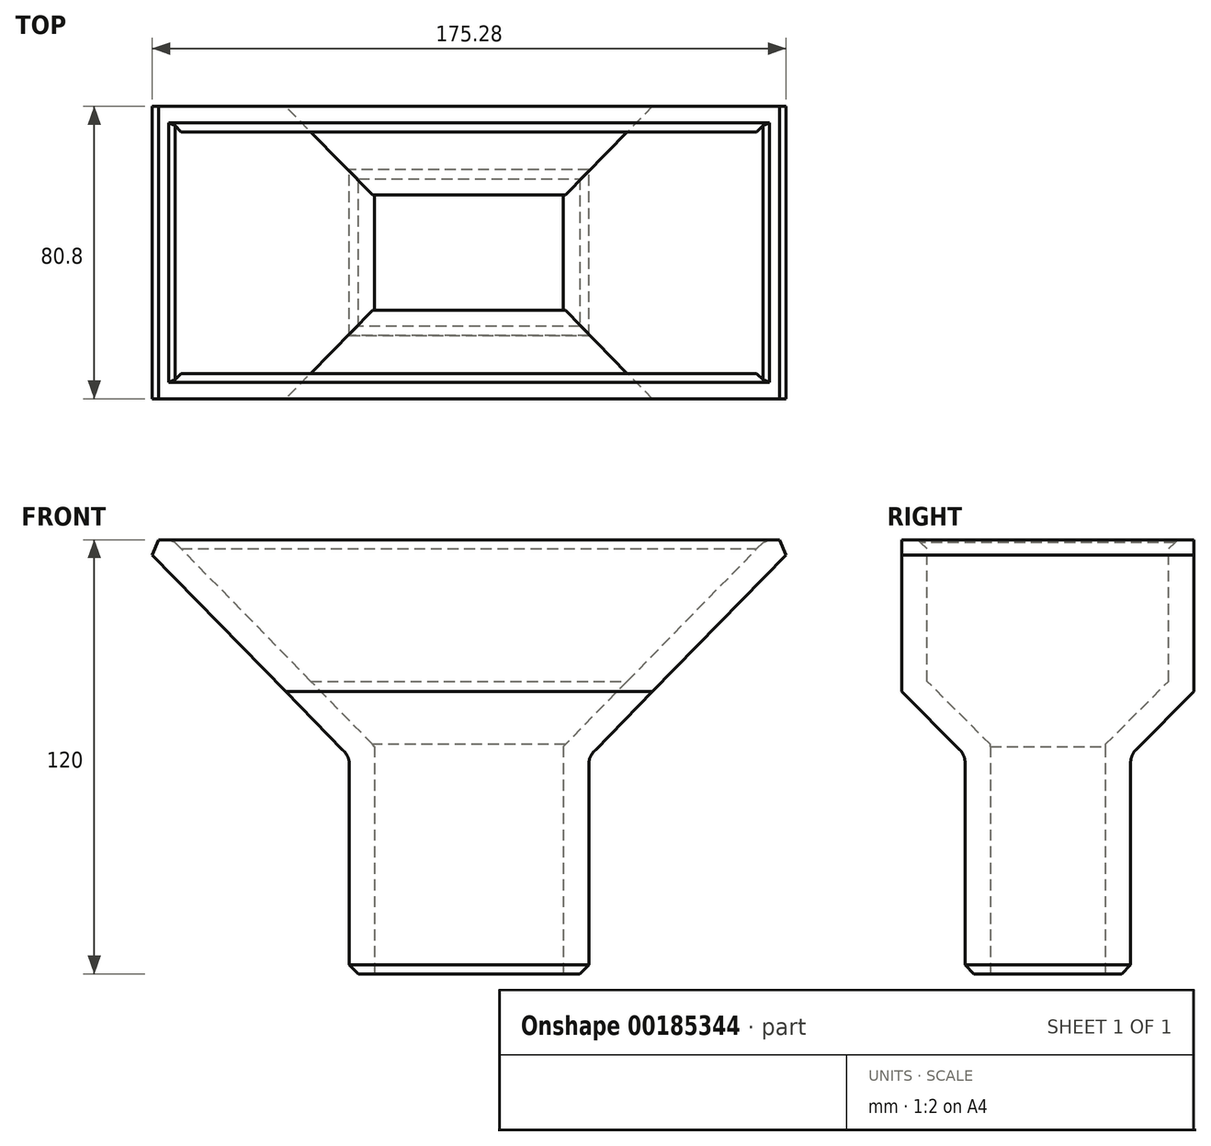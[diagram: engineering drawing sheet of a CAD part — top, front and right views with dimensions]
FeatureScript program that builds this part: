
annotation { "Feature Type Name" : "Feature", "Feature Type Description" : "" }
export const myFeature = defineFeature(function(context is Context, id is Id, definition is map)
    precondition{}
    {
        {
            var Q0;
            Q0=qCreatedBy(makeId("Front.planeOp"),FACE);
            var sketch = newSketch(context, id + "F0", { "sketchPlane" : qUnion([Q0])});
            skLineSegment(sketch, "E0.bottom", {"start": v(-33.1, 0) * mm, "end": v(33.1, 0) * mm});
            skLineSegment(sketch, "E0.top", {"start": v(-33.1, -60) * mm, "end": v(33.1, -60) * mm});
            skLineSegment(sketch, "E0.left", {"start": v(-33.1, 0) * mm, "end": v(-33.1, -60) * mm});
            skLineSegment(sketch, "E0.right", {"start": v(33.1, 0) * mm, "end": v(33.1, -60) * mm});
            skPoint(sketch, "E1", {"position": v(0, 0) * mm});
            skLineSegment(sketch, "E2", {"start": v(-33.1, 0) * mm, "end": v(-91.8, 60) * mm});
            skLineSegment(sketch, "E3", {"start": v(33.1, 0) * mm, "end": v(91.8, 60) * mm});
            skLineSegment(sketch, "E4", {"start": v(91.8, 60) * mm, "end": v(-91.8, 60) * mm});
            skSolve(sketch);
        }
        {
            var Q0;
            Q0=makeQuery(id+"F0.imprint","IMPRINT",FACE,{"disambiguationData":[TD([[makeQuery(id+"F0.imprint","IMPRINT",EDGE,{"derivedFrom":sQuery(id+"F0.wireOp",EDGE,"E0.bottom")}),1.0]])]});
            extrude(context, id + "F1", {"entities" : qUnion([Q0]), "depth" : (50.8 + 30) * mm, "symmetric" : true});
        }
        {
            var Q0;
            Q0=makeQuery(id+"F0.imprint","IMPRINT",FACE,{"disambiguationData":[TD([[makeQuery(id+"F0.imprint","IMPRINT",EDGE,{"derivedFrom":sQuery(id+"F0.wireOp",EDGE,"E0.bottom")}),-1.0]])]});
            extrude(context, id + "F2", {"entities" : qUnion([Q0]), "operationType" : NewBodyOperationType.ADD, "depth" : (50.8 - 5) * mm, "symmetric" : true});
        }
        {
            var Q0;
            Q0=makeQuery(id+"F1.opExtrude","CAP_EDGE",EDGE,{"disambiguationData":[OSD([sQuery(id+"F0.wireOp",EDGE,"E0.bottom")])],"isStart":false});
            var Q1;
            Q1=makeQuery(id+"F1.opExtrude","CAP_EDGE",EDGE,{"disambiguationData":[OSD([sQuery(id+"F0.wireOp",EDGE,"E0.bottom")])],"isStart":true});
            chamfer(context, id + "F3", {"entities" : qUnion([Q0, Q1]), "width" : 18 * mm, "tangentPropagation" : true});
        }
        {
            var Q0;
            Q0=makeQuery(id+"F2.opExtrude","SWEPT_FACE",FACE,{"disambiguationData":[OSD([sQuery(id+"F0.wireOp",EDGE,"E0.top")])]});
            var Q1;
            Q1=makeQuery(id+"F1.opExtrude","SWEPT_FACE",FACE,{"disambiguationData":[OSD([sQuery(id+"F0.wireOp",EDGE,"E4")])]});
            shell(context, id + "F4", {"entities" : qUnion([Q0, Q1]), "thickness" : 7 * mm});
        }
        {
            var Q0;
            Q0=makeQuery(id+"F2.opExtrude","CAP_EDGE",EDGE,{"disambiguationData":[OSD([sQuery(id+"F0.wireOp",EDGE,"E0.top")])],"isStart":true});
            var Q1;
            Q1=makeQuery(id+"F2.opExtrude","SWEPT_EDGE",EDGE,{"disambiguationData":[OSD([sQuery(id+"F0.wireOp",EDGE,"E0.top"),sQuery(id+"F0.wireOp",EDGE,"E0.right")])]});
            var Q2;
            Q2=makeQuery(id+"F2.opExtrude","CAP_EDGE",EDGE,{"disambiguationData":[OSD([sQuery(id+"F0.wireOp",EDGE,"E0.top")])],"isStart":false});
            var Q3;
            Q3=makeQuery(id+"F2.opExtrude","SWEPT_EDGE",EDGE,{"disambiguationData":[OSD([sQuery(id+"F0.wireOp",EDGE,"E0.top"),sQuery(id+"F0.wireOp",EDGE,"E0.left")])]});
            chamfer(context, id + "F5", {"entities" : qUnion([Q0, Q1, Q2, Q3]), "width" : 2.5 * mm, "tangentPropagation" : true});
        }
        {
            var Q0;
            {var subQ0=sQuery(id+"F0.wireOp",EDGE,"E4");Q0=makeQuery(id+"F4.opShell","OFFSET_EDGE",EDGE,{"disambiguationData":[OSD([subQ0]),TDD([makeQuery(id+"F1.opExtrude","CAP_EDGE",EDGE,{"disambiguationData":[OSD([subQ0])],"isStart":true})])]});}
            var Q1;
            Q1=makeQuery(id+"F4.opShell","OFFSET_EDGE",EDGE,{"disambiguationData":[OSD([sQuery(id+"F0.wireOp",EDGE,"E3"),sQuery(id+"F0.wireOp",EDGE,"E4")])]});
            var Q2;
            {var subQ0=sQuery(id+"F0.wireOp",EDGE,"E4");Q2=makeQuery(id+"F4.opShell","OFFSET_EDGE",EDGE,{"disambiguationData":[OSD([subQ0]),TDD([makeQuery(id+"F1.opExtrude","CAP_EDGE",EDGE,{"disambiguationData":[OSD([subQ0])],"isStart":false})])]});}
            var Q3;
            Q3=makeQuery(id+"F4.opShell","OFFSET_EDGE",EDGE,{"disambiguationData":[OSD([sQuery(id+"F0.wireOp",EDGE,"E2"),sQuery(id+"F0.wireOp",EDGE,"E4")])]});
            var Q4;
            Q4=makeQuery(id+"F1.opExtrude","SWEPT_EDGE",EDGE,{"disambiguationData":[OSD([sQuery(id+"F0.wireOp",EDGE,"E3"),sQuery(id+"F0.wireOp",EDGE,"E4")])]});
            var Q5;
            Q5=makeQuery(id+"F1.opExtrude","SWEPT_EDGE",EDGE,{"disambiguationData":[OSD([sQuery(id+"F0.wireOp",EDGE,"E2"),sQuery(id+"F0.wireOp",EDGE,"E4")])]});
            chamfer(context, id + "F6", {"entities" : qUnion([Q0, Q1, Q2, Q3, Q4, Q5]), "width" : 2.5 * mm, "tangentPropagation" : true});
        }
        {
            var Q0;
            {var subQ0=sQuery(id+"F0.wireOp",EDGE,"E0.bottom");Q0=makeQuery(id+"F3.opChamfer","BLEND_EDGE",EDGE,{"blendedFrom":[makeQuery(id+"F1.opExtrude","CAP_EDGE",EDGE,{"disambiguationData":[OSD([subQ0])],"isStart":false}),makeQuery(id+"F2.opExtrude","CAP_FACE",FACE,{"disambiguationData":[OSD([subQ0,sQuery(id+"F0.wireOp",EDGE,"E0.top"),sQuery(id+"F0.wireOp",EDGE,"E0.left"),sQuery(id+"F0.wireOp",EDGE,"E0.right")])],"isStart":false})],"blendedInto":[makeQuery(id+"F2.opExtrude","CAP_FACE",FACE,{"disambiguationData":[OSD([subQ0,sQuery(id+"F0.wireOp",EDGE,"E0.top"),sQuery(id+"F0.wireOp",EDGE,"E0.left"),sQuery(id+"F0.wireOp",EDGE,"E0.right")])],"isStart":false})]});}
            var Q1;
            {var subQ0=sQuery(id+"F0.wireOp",EDGE,"E3");var subQ1=sQuery(id+"F0.wireOp",EDGE,"E0.right");var subQ2=sQuery(id+"F0.wireOp",EDGE,"E0.bottom");Q1=makeQuery(id+"F2.boolean.opBoolean","MERGE",EDGE,{"derivedFrom":[makeQuery(id+"F1.opExtrude","SWEPT_EDGE",EDGE,{"disambiguationData":[OSD([subQ2,subQ1,subQ0])]}),makeQuery(id+"F2.opExtrude","SWEPT_EDGE",EDGE,{"disambiguationData":[OSD([subQ2,subQ1,subQ0])]})]});}
            var Q2;
            {var subQ0=sQuery(id+"F0.wireOp",EDGE,"E2");var subQ1=sQuery(id+"F0.wireOp",EDGE,"E0.left");var subQ2=sQuery(id+"F0.wireOp",EDGE,"E0.bottom");Q2=makeQuery(id+"F2.boolean.opBoolean","MERGE",EDGE,{"derivedFrom":[makeQuery(id+"F1.opExtrude","SWEPT_EDGE",EDGE,{"disambiguationData":[OSD([subQ2,subQ1,subQ0])]}),makeQuery(id+"F2.opExtrude","SWEPT_EDGE",EDGE,{"disambiguationData":[OSD([subQ2,subQ1,subQ0])]})]});}
            var Q3;
            {var subQ0=sQuery(id+"F0.wireOp",EDGE,"E0.bottom");Q3=makeQuery(id+"F3.opChamfer","BLEND_EDGE",EDGE,{"blendedFrom":[makeQuery(id+"F1.opExtrude","CAP_EDGE",EDGE,{"disambiguationData":[OSD([subQ0])],"isStart":true}),makeQuery(id+"F2.opExtrude","CAP_FACE",FACE,{"disambiguationData":[OSD([subQ0,sQuery(id+"F0.wireOp",EDGE,"E0.top"),sQuery(id+"F0.wireOp",EDGE,"E0.left"),sQuery(id+"F0.wireOp",EDGE,"E0.right")])],"isStart":true})],"blendedInto":[makeQuery(id+"F2.opExtrude","CAP_FACE",FACE,{"disambiguationData":[OSD([subQ0,sQuery(id+"F0.wireOp",EDGE,"E0.top"),sQuery(id+"F0.wireOp",EDGE,"E0.left"),sQuery(id+"F0.wireOp",EDGE,"E0.right")])],"isStart":true})]});}
            var Q4;
            Q4=makeQuery(id+"F3.opChamfer","BLEND_EDGE",EDGE,{"blendedFrom":[makeQuery(id+"F1.opExtrude","CAP_EDGE",EDGE,{"disambiguationData":[OSD([sQuery(id+"F0.wireOp",EDGE,"E0.bottom")])],"isStart":true}),makeQuery(id+"F2.opExtrude","SWEPT_FACE",FACE,{"disambiguationData":[OSD([sQuery(id+"F0.wireOp",EDGE,"E0.right")])]})],"blendedInto":[makeQuery(id+"F2.opExtrude","SWEPT_FACE",FACE,{"disambiguationData":[OSD([sQuery(id+"F0.wireOp",EDGE,"E0.right")])]})]});
            var Q5;
            Q5=makeQuery(id+"F3.opChamfer","BLEND_EDGE",EDGE,{"blendedFrom":[makeQuery(id+"F1.opExtrude","CAP_EDGE",EDGE,{"disambiguationData":[OSD([sQuery(id+"F0.wireOp",EDGE,"E0.bottom")])],"isStart":true}),makeQuery(id+"F2.opExtrude","SWEPT_FACE",FACE,{"disambiguationData":[OSD([sQuery(id+"F0.wireOp",EDGE,"E0.left")])]})],"blendedInto":[makeQuery(id+"F2.opExtrude","SWEPT_FACE",FACE,{"disambiguationData":[OSD([sQuery(id+"F0.wireOp",EDGE,"E0.left")])]})]});
            var Q6;
            Q6=makeQuery(id+"F3.opChamfer","BLEND_EDGE",EDGE,{"blendedFrom":[makeQuery(id+"F1.opExtrude","CAP_EDGE",EDGE,{"disambiguationData":[OSD([sQuery(id+"F0.wireOp",EDGE,"E0.bottom")])],"isStart":false}),makeQuery(id+"F2.opExtrude","SWEPT_FACE",FACE,{"disambiguationData":[OSD([sQuery(id+"F0.wireOp",EDGE,"E0.left")])]})],"blendedInto":[makeQuery(id+"F2.opExtrude","SWEPT_FACE",FACE,{"disambiguationData":[OSD([sQuery(id+"F0.wireOp",EDGE,"E0.left")])]})]});
            var Q7;
            Q7=makeQuery(id+"F3.opChamfer","BLEND_EDGE",EDGE,{"blendedFrom":[makeQuery(id+"F1.opExtrude","CAP_EDGE",EDGE,{"disambiguationData":[OSD([sQuery(id+"F0.wireOp",EDGE,"E0.bottom")])],"isStart":false}),makeQuery(id+"F2.opExtrude","SWEPT_FACE",FACE,{"disambiguationData":[OSD([sQuery(id+"F0.wireOp",EDGE,"E0.right")])]})],"blendedInto":[makeQuery(id+"F2.opExtrude","SWEPT_FACE",FACE,{"disambiguationData":[OSD([sQuery(id+"F0.wireOp",EDGE,"E0.right")])]})]});
            fillet(context, id + "F7", {"entities" : qUnion([Q0, Q1, Q2, Q3, Q4, Q5, Q6, Q7]), "radius" : 5 * mm, "tangentPropagation" : true, "allowEdgeOverflow" : false});
        }
    });
